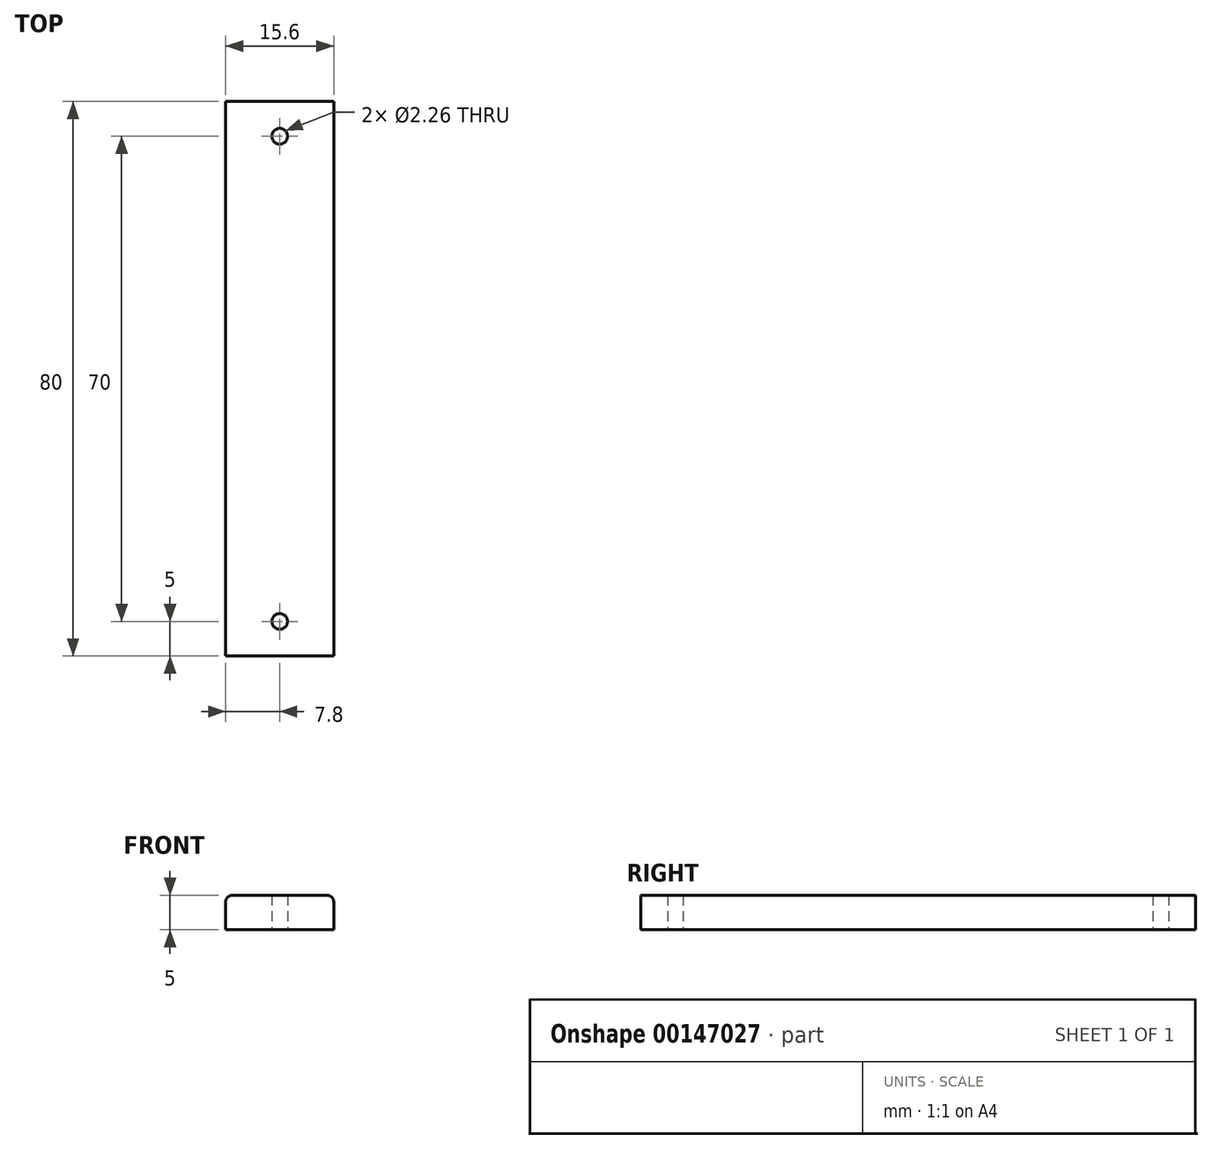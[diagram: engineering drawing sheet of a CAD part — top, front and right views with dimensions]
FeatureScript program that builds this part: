
annotation { "Feature Type Name" : "Feature", "Feature Type Description" : "" }
export const myFeature = defineFeature(function(context is Context, id is Id, definition is map)
    precondition{}
    {
        {
            var Q0;
            Q0=qCreatedBy(makeId("Front.planeOp"),FACE);
            var sketch = newSketch(context, id + "F0", { "sketchPlane" : qUnion([Q0])});
            skPoint(sketch, "E0.middle", {"position": v(0, 0) * mm});
            skLineSegment(sketch, "E1.bottom", {"start": v(7.8, 3.07) * mm, "end": v(-7.8, 3.07) * mm});
            skPoint(sketch, "E2.orphan", {"position": v(10.6, 10.84) * mm});
            skPoint(sketch, "E3.orphan", {"position": v(-10.6, 10.84) * mm});
            skPoint(sketch, "E4.orphan", {"position": v(-10.6, -10.84) * mm});
            skPoint(sketch, "E5.orphan", {"position": v(10.6, -10.84) * mm});
            skPoint(sketch, "E6", {"position": v(0, 3.07) * mm});
            skLineSegment(sketch, "E7.0", {"start": v(7.8, 3.07) * mm, "end": v(7.8, 8.07) * mm});
            skLineSegment(sketch, "E8.0", {"start": v(-7.8, 3.07) * mm, "end": v(-7.8, 8.07) * mm});
            skLineSegment(sketch, "E9", {"start": v(-7.8, 8.07) * mm, "end": v(7.8, 8.07) * mm});
            skPoint(sketch, "E0.right.end.orphan", {"position": v(-9.5, 1.37) * mm});
            skPoint(sketch, "E10.orphan", {"position": v(-9.5, -1.37) * mm});
            skPoint(sketch, "E1.top.end.orphan", {"position": v(-7.8, -3.07) * mm});
            skPoint(sketch, "E1.left.end.orphan", {"position": v(7.8, -3.07) * mm});
            skPoint(sketch, "E11.start.orphan", {"position": v(9.5, -1.37) * mm});
            skPoint(sketch, "E12.trimOffspring.start.orphan", {"position": v(9.5, 1.37) * mm});
            skSolve(sketch);
        }
        {
            var Q0;
            Q0 = qSketchRegion(id + "F0", true);
            extrude(context, id + "F1", {"entities" : qUnion([Q0]), "endBound" : BoundingType.SYMMETRIC, "depth" : 80 * mm});
        }
        {
            var Q0;
            Q0=makeQuery(id+"F1.opExtrude","SWEPT_EDGE",EDGE,{"disambiguationData":[OSD([sQuery(id+"F0.wireOp",EDGE,"E7.0"),sQuery(id+"F0.wireOp",EDGE,"E9")])]});
            fillet(context, id + "F2", {"entities" : qUnion([Q0]), "radius" : 1 * mm, "tangentPropagation" : true, "allowEdgeOverflow" : false});
        }
        {
            var Q0;
            Q0=makeQuery(id+"F1.opExtrude","SWEPT_EDGE",EDGE,{"disambiguationData":[OSD([sQuery(id+"F0.wireOp",EDGE,"E8.0"),sQuery(id+"F0.wireOp",EDGE,"E9")])]});
            fillet(context, id + "F3", {"entities" : qUnion([Q0]), "radius" : 1 * mm, "tangentPropagation" : true, "allowEdgeOverflow" : false});
        }
        {
            var Q0;
            Q0=qCreatedBy(makeId("Front.planeOp"),FACE);
            cPlane(context, id + "F4", {"entities" : qUnion([Q0]), "cplaneType" : CPlaneType.OFFSET, "offset" : 35 * mm, "width" : 150 * mm, "height" : 150 * mm});
        }
        {
            var Q0;
            Q0=qCreatedBy(makeId("Front.planeOp"),FACE);
            cPlane(context, id + "F5", {"entities" : qUnion([Q0]), "cplaneType" : CPlaneType.OFFSET, "offset" : 35 * mm, "oppositeDirection" : true, "width" : 150 * mm, "height" : 150 * mm});
        }
        {
            var Q0;
            Q0=qCreatedBy(makeId("Top.planeOp"),FACE);
            var sketch = newSketch(context, id + "F6", { "sketchPlane" : qUnion([Q0])});
            skLineSegment(sketch, "E13", {"start": v(40.72, -35) * mm, "end": v(-61.86, -35) * mm});
            skLineSegment(sketch, "E14", {"start": v(0, 38.57) * mm, "end": v(0, -64) * mm});
            skLineSegment(sketch, "E15", {"start": v(40.72, 35) * mm, "end": v(-61.86, 35) * mm});
            skPoint(sketch, "E16", {"position": v(0, -35) * mm});
            skPoint(sketch, "E17", {"position": v(0, 35) * mm});
            skSolve(sketch);
        }
        {
            var Q0;
            Q0=sQuery(id+"F6.wireOp",VERTEX,"E16");
            var Q1;
            Q1=makeQuery(id+"F1.opExtrude","SWEPT_BODY",BODY,{"disambiguationData":[OSD([sQuery(id+"F0.wireOp",EDGE,"E1.bottom"),sQuery(id+"F0.wireOp",EDGE,"E7.0"),sQuery(id+"F0.wireOp",EDGE,"E8.0"),sQuery(id+"F0.wireOp",EDGE,"E9")])]});
            hole(context, id + "F7", {"style" : HoleStyle.SIMPLE, "endStyle" : HoleEndStyle.THROUGH, "holeDiameter" : 2.26 * mm, "startFromSketch" : true, "locations" : qUnion([Q0]), "scope" : qUnion([Q1]), "isTappedThrough" : true});
        }
        {
            var Q0;
            Q0=sQuery(id+"F6.wireOp",VERTEX,"E16");
            var Q1;
            Q1=makeQuery(id+"F1.opExtrude","SWEPT_BODY",BODY,{"disambiguationData":[OSD([sQuery(id+"F0.wireOp",EDGE,"E1.bottom"),sQuery(id+"F0.wireOp",EDGE,"E7.0"),sQuery(id+"F0.wireOp",EDGE,"E8.0"),sQuery(id+"F0.wireOp",EDGE,"E9")])]});
            hole(context, id + "F8", {"style" : HoleStyle.SIMPLE, "endStyle" : HoleEndStyle.THROUGH, "oppositeDirection" : true, "holeDiameter" : 2.26 * mm, "startFromSketch" : true, "locations" : qUnion([Q0]), "scope" : qUnion([Q1]), "isTappedThrough" : true});
        }
        {
            var Q0;
            Q0=sQuery(id+"F6.wireOp",VERTEX,"E17");
            var Q1;
            Q1=makeQuery(id+"F1.opExtrude","SWEPT_BODY",BODY,{"disambiguationData":[OSD([sQuery(id+"F0.wireOp",EDGE,"E1.bottom"),sQuery(id+"F0.wireOp",EDGE,"E7.0"),sQuery(id+"F0.wireOp",EDGE,"E8.0"),sQuery(id+"F0.wireOp",EDGE,"E9")])]});
            hole(context, id + "F9", {"style" : HoleStyle.SIMPLE, "endStyle" : HoleEndStyle.THROUGH, "holeDiameter" : 2.26 * mm, "startFromSketch" : true, "locations" : qUnion([Q0]), "scope" : qUnion([Q1]), "isTappedThrough" : true});
        }
        {
            var Q0;
            Q0=sQuery(id+"F6.wireOp",VERTEX,"E17");
            var Q1;
            Q1=makeQuery(id+"F1.opExtrude","SWEPT_BODY",BODY,{"disambiguationData":[OSD([sQuery(id+"F0.wireOp",EDGE,"E1.bottom"),sQuery(id+"F0.wireOp",EDGE,"E7.0"),sQuery(id+"F0.wireOp",EDGE,"E8.0"),sQuery(id+"F0.wireOp",EDGE,"E9")])]});
            hole(context, id + "F10", {"style" : HoleStyle.SIMPLE, "endStyle" : HoleEndStyle.THROUGH, "oppositeDirection" : true, "holeDiameter" : 2.26 * mm, "startFromSketch" : true, "locations" : qUnion([Q0]), "scope" : qUnion([Q1]), "isTappedThrough" : true});
        }
    });
